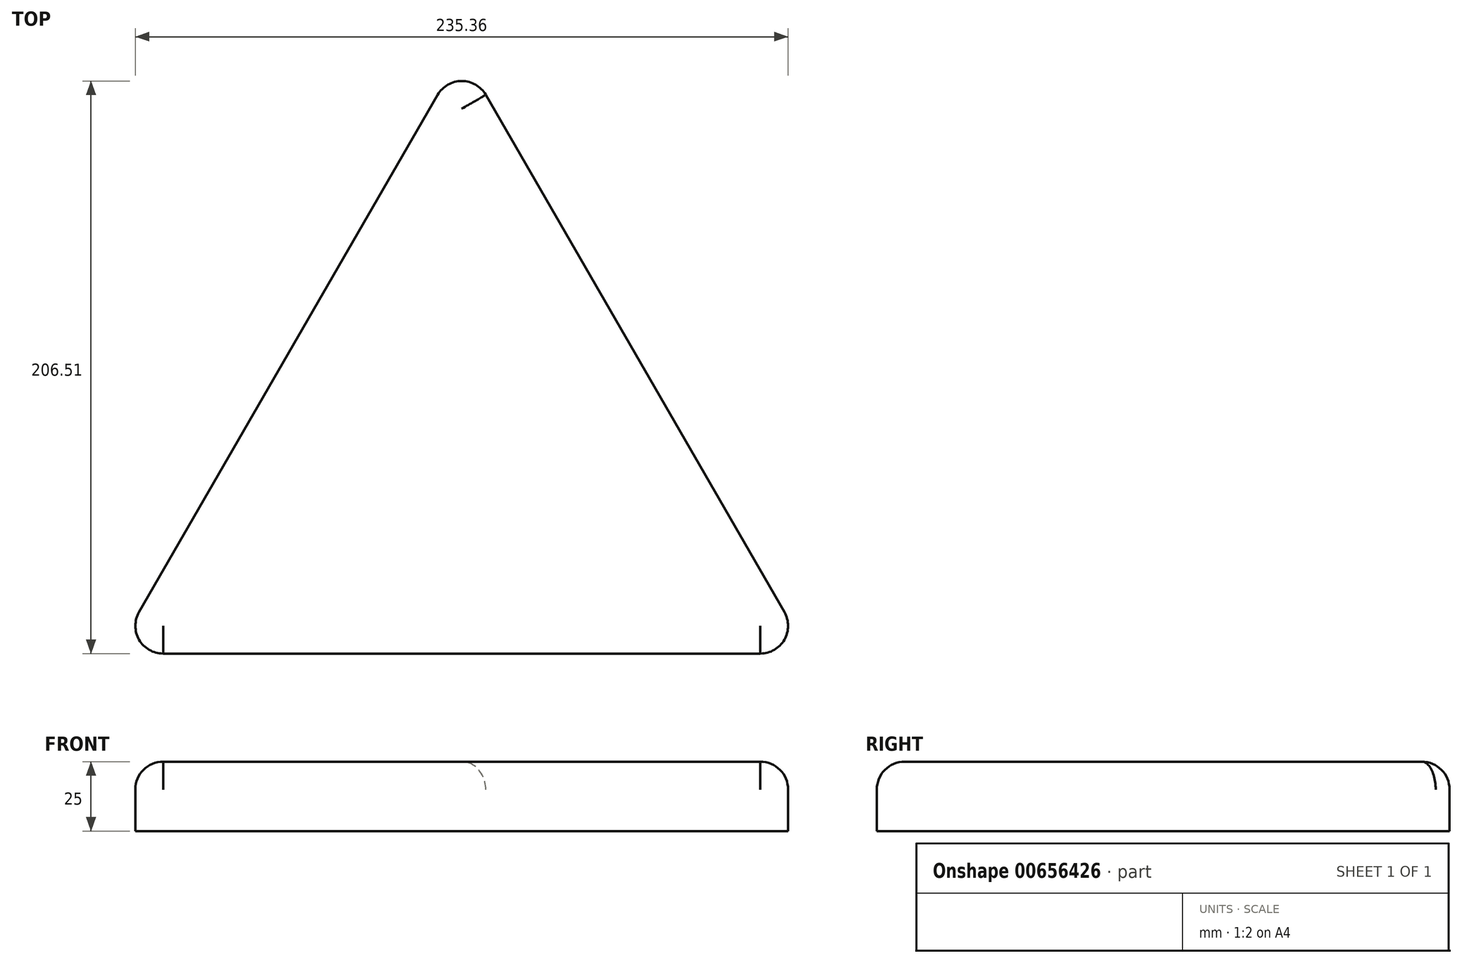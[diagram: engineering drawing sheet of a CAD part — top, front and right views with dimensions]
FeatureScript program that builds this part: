
annotation { "Feature Type Name" : "Feature", "Feature Type Description" : "" }
export const myFeature = defineFeature(function(context is Context, id is Id, definition is map)
    precondition{}
    {
        {
            var Q0;
            Q0=qCreatedBy(makeId("Top.planeOp"),FACE);
            var sketch = newSketch(context, id + "F0", { "sketchPlane" : qUnion([Q0])});
            skLineSegment(sketch, "E0", {"start": v(0, 0) * mm, "end": v(125, -216.5) * mm});
            skLineSegment(sketch, "E1", {"start": v(125, -216.5) * mm, "end": v(-125, -216.5) * mm});
            skLineSegment(sketch, "E2", {"start": v(-125, -216.5) * mm, "end": v(0, 0) * mm});
            skSolve(sketch);
        }
        {
            var Q0;
            Q0 = qSketchRegion(id + "F0", true);
            extrude(context, id + "F1", {"entities" : qUnion([Q0]), "depth" : 25 * mm, "offsetDistance" : 25 * mm});
        }
        {
            var Q0;
            Q0=makeQuery(id+"F1.opExtrude","CAP_EDGE",EDGE,{"disambiguationData":[OSD([sQuery(id+"F0.wireOp",EDGE,"E1")])],"isStart":false});
            fillet(context, id + "F2", {"entities" : qUnion([Q0]), "radius" : 10 * mm, "tangentPropagation" : true, "allowEdgeOverflow" : false});
        }
        {
            var Q0;
            Q0=makeQuery(id+"F1.opExtrude","CAP_EDGE",EDGE,{"disambiguationData":[OSD([sQuery(id+"F0.wireOp",EDGE,"E0")])],"isStart":false});
            fillet(context, id + "F3", {"entities" : qUnion([Q0]), "radius" : 10 * mm, "tangentPropagation" : true, "allowEdgeOverflow" : false});
        }
        {
            var Q0;
            Q0=makeQuery(id+"F1.opExtrude","CAP_EDGE",EDGE,{"disambiguationData":[OSD([sQuery(id+"F0.wireOp",EDGE,"E2")])],"isStart":false});
            fillet(context, id + "F4", {"entities" : qUnion([Q0]), "radius" : 10 * mm, "tangentPropagation" : true, "allowEdgeOverflow" : false});
        }
        {
            var Q0;
            Q0=qCreatedBy(makeId("Top.planeOp"),FACE);
            var sketch = newSketch(context, id + "F5", { "sketchPlane" : qUnion([Q0])});
            skCircle(sketch, "E3", {"center": v(-437, -381.23) * mm, "radius": 5 * mm});
            skSolve(sketch);
        }
    });
